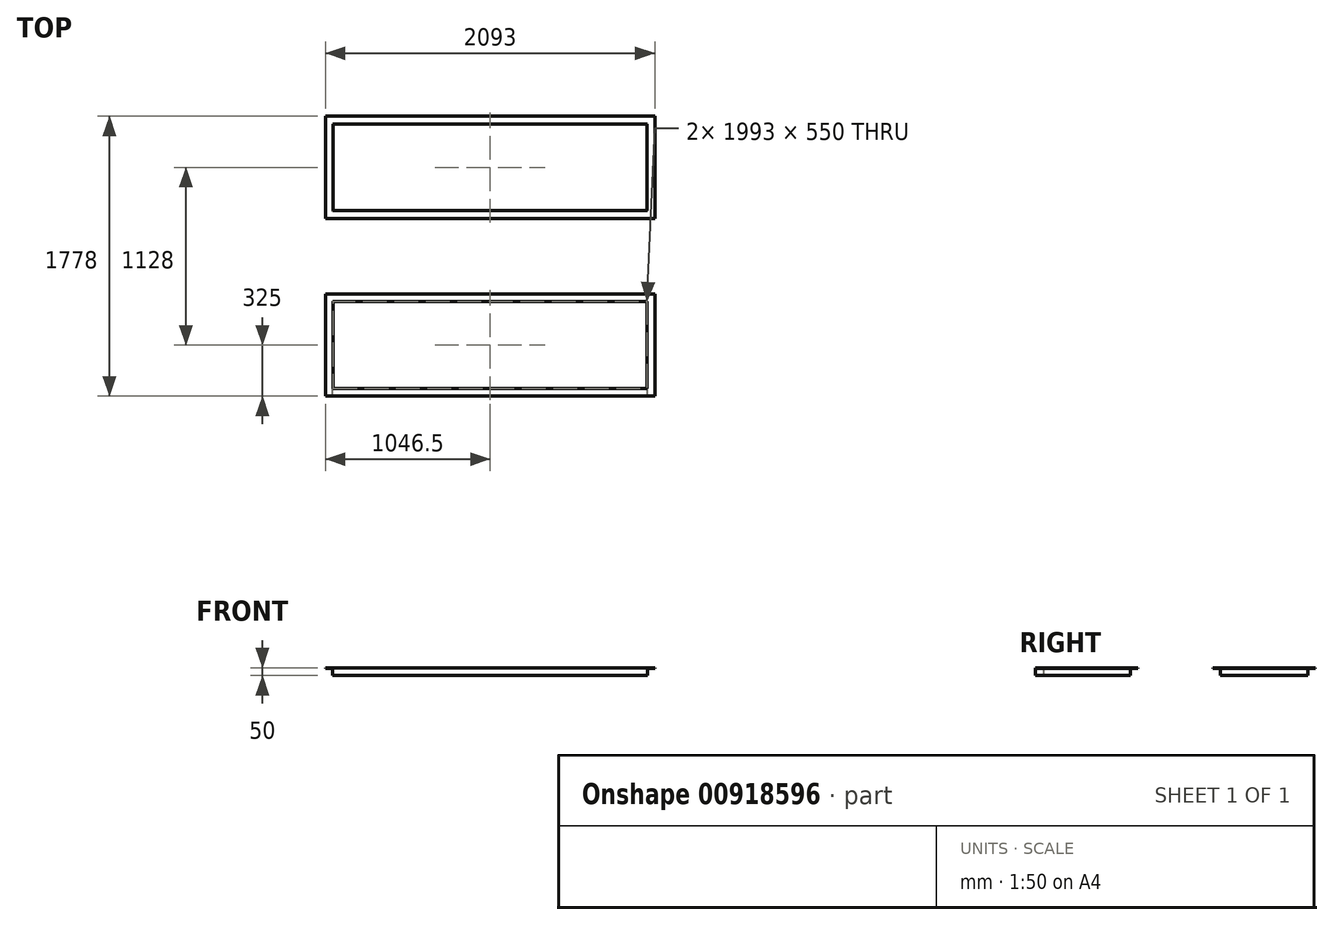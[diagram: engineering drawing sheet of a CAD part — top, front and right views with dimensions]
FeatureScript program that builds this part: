
annotation { "Feature Type Name" : "Feature", "Feature Type Description" : "" }
export const myFeature = defineFeature(function(context is Context, id is Id, definition is map)
    precondition{}
    {
        {
            var Q0;
            Q0=qCreatedBy(makeId("Top.planeOp"),FACE);
            var sketch = newSketch(context, id + "F0", { "sketchPlane" : qUnion([Q0])});
            skLineSegment(sketch, "E0.bottom", {"start": v(0, 0) * mm, "end": v(-1993, 0) * mm});
            skLineSegment(sketch, "E0.top", {"start": v(0, 550) * mm, "end": v(-1993, 550) * mm});
            skLineSegment(sketch, "E0.left", {"start": v(0, 0) * mm, "end": v(0, 550) * mm});
            skLineSegment(sketch, "E0.right", {"start": v(-1993, 0) * mm, "end": v(-1993, 550) * mm});
            skLineSegment(sketch, "E1.bottom", {"start": v(-2043, 600) * mm, "end": v(50, 600) * mm});
            skLineSegment(sketch, "E1.top", {"start": v(-2043, -50) * mm, "end": v(50, -50) * mm});
            skLineSegment(sketch, "E1.left", {"start": v(-2043, 600) * mm, "end": v(-2043, -50) * mm});
            skLineSegment(sketch, "E1.right", {"start": v(50, 600) * mm, "end": v(50, -50) * mm});
            skLineSegment(sketch, "E2.bottom", {"start": v(-1993, 1128) * mm, "end": v(0, 1128) * mm});
            skLineSegment(sketch, "E2.top", {"start": v(-1993, 1678) * mm, "end": v(0, 1678) * mm});
            skLineSegment(sketch, "E2.left", {"start": v(-1993, 1128) * mm, "end": v(-1993, 1678) * mm});
            skLineSegment(sketch, "E2.right", {"start": v(0, 1128) * mm, "end": v(0, 1678) * mm});
            skLineSegment(sketch, "E3.bottom", {"start": v(-2043, 1078) * mm, "end": v(50, 1078) * mm});
            skLineSegment(sketch, "E3.top", {"start": v(-2043, 1728) * mm, "end": v(50, 1728) * mm});
            skLineSegment(sketch, "E3.left", {"start": v(-2043, 1078) * mm, "end": v(-2043, 1728) * mm});
            skLineSegment(sketch, "E3.right", {"start": v(50, 1078) * mm, "end": v(50, 1728) * mm});
            skSolve(sketch);
        }
        {
            var Q0;
            Q0 = qSketchRegion(id + "F0", true);
            extrude(context, id + "F1", {"entities" : qUnion([Q0]), "depth" : 50 * mm, "offsetDistance" : 25 * mm});
        }
        {
            var Q0;
            Q0=makeQuery(id+"F1.opExtrude","SWEPT_FACE",FACE,{"disambiguationData":[OSD([sQuery(id+"F0.wireOp",EDGE,"E3.left")])]});
            var sketch = newSketch(context, id + "F2", { "sketchPlane" : qUnion([Q0])});
            skLineSegment(sketch, "E4.bottom", {"start": v(-1728, 46) * mm, "end": v(-1682, 46) * mm});
            skLineSegment(sketch, "E4.top", {"start": v(-1728, 0) * mm, "end": v(-1682, 0) * mm});
            skLineSegment(sketch, "E4.left", {"start": v(-1728, 46) * mm, "end": v(-1728, 0) * mm});
            skLineSegment(sketch, "E4.right", {"start": v(-1682, 46) * mm, "end": v(-1682, 0) * mm});
            skLineSegment(sketch, "E5.bottom", {"start": v(-1078, 46) * mm, "end": v(-1124, 46) * mm});
            skLineSegment(sketch, "E5.top", {"start": v(-1078, 0) * mm, "end": v(-1124, 0) * mm});
            skLineSegment(sketch, "E5.left", {"start": v(-1078, 46) * mm, "end": v(-1078, 0) * mm});
            skLineSegment(sketch, "E5.right", {"start": v(-1124, 46) * mm, "end": v(-1124, 0) * mm});
            skLineSegment(sketch, "E6.0.0", {"start": v(-600, 0) * mm, "end": v(50, 0) * mm});
            skLineSegment(sketch, "E6.0.1", {"start": v(50, 0) * mm, "end": v(50, 50) * mm});
            skLineSegment(sketch, "E6.0.2", {"start": v(50, 50) * mm, "end": v(-600, 50) * mm});
            skLineSegment(sketch, "E6.0.3", {"start": v(-600, 50) * mm, "end": v(-600, 0) * mm});
            skLineSegment(sketch, "E7.bottom", {"start": v(-600, 46) * mm, "end": v(-554, 46) * mm});
            skLineSegment(sketch, "E7.top", {"start": v(-600, 0) * mm, "end": v(-554, 0) * mm});
            skLineSegment(sketch, "E7.left", {"start": v(-600, 46) * mm, "end": v(-600, 0) * mm});
            skLineSegment(sketch, "E7.right", {"start": v(-554, 46) * mm, "end": v(-554, 0) * mm});
            skLineSegment(sketch, "E8.bottom", {"start": v(4, 0) * mm, "end": v(50, 0) * mm});
            skLineSegment(sketch, "E8.top", {"start": v(4, 46) * mm, "end": v(50, 46) * mm});
            skLineSegment(sketch, "E8.left", {"start": v(4, 0) * mm, "end": v(4, 46) * mm});
            skLineSegment(sketch, "E8.right", {"start": v(50, 0) * mm, "end": v(50, 46) * mm});
            skSolve(sketch);
        }
        {
            var Q0;
            Q0=makeQuery(id+"F2.imprint","IMPRINT",FACE,{"disambiguationData":[TD([[makeQuery(id+"F2.imprint","IMPRINT",EDGE,{"derivedFrom":sQuery(id+"F2.wireOp",EDGE,"E4.bottom")}),-1.0]])]});
            var Q1;
            Q1=makeQuery(id+"F2.imprint","IMPRINT",FACE,{"disambiguationData":[TD([[makeQuery(id+"F2.imprint","IMPRINT",EDGE,{"derivedFrom":sQuery(id+"F2.wireOp",EDGE,"E5.bottom")}),1.0]])]});
            var Q2;
            Q2=makeQuery(id+"F2.imprint","IMPRINT",FACE,{"disambiguationData":[TD([[makeQuery(id+"F2.imprint","IMPRINT",EDGE,{"derivedFrom":sQuery(id+"F2.wireOp",EDGE,"E7.bottom")}),-1.0]])]});
            var Q3;
            Q3=makeQuery(id+"F2.imprint","IMPRINT",FACE,{"disambiguationData":[TD([[makeQuery(id+"F2.imprint","IMPRINT",EDGE,{"derivedFrom":sQuery(id+"F2.wireOp",EDGE,"E8.bottom")}),1.0]])]});
            extrude(context, id + "F3", {"entities" : qUnion([Q0, Q1, Q2, Q3]), "operationType" : NewBodyOperationType.REMOVE, "oppositeDirection" : true, "depth" : 3000 * mm, "offsetDistance" : 25 * mm});
        }
        {
            var Q0;
            Q0=makeQuery(id+"F3.boolean.opBoolean","COPY",FACE,{"derivedFrom":makeQuery(id+"F3.opExtrude","SWEPT_FACE",FACE,{"disambiguationData":[OSD([sQuery(id+"F2.wireOp",EDGE,"E4.right")])]})});
            var sketch = newSketch(context, id + "F4", { "sketchPlane" : qUnion([Q0])});
            skLineSegment(sketch, "E9.bottom", {"start": v(-50, 46) * mm, "end": v(-4, 46) * mm});
            skLineSegment(sketch, "E9.top", {"start": v(-50, 0) * mm, "end": v(-4, 0) * mm});
            skLineSegment(sketch, "E9.left", {"start": v(-50, 46) * mm, "end": v(-50, 0) * mm});
            skLineSegment(sketch, "E9.right", {"start": v(-4, 46) * mm, "end": v(-4, 0) * mm});
            skLineSegment(sketch, "E10.bottom", {"start": v(2043, 46) * mm, "end": v(1997, 46) * mm});
            skLineSegment(sketch, "E10.top", {"start": v(2043, 0) * mm, "end": v(1997, 0) * mm});
            skLineSegment(sketch, "E10.left", {"start": v(2043, 46) * mm, "end": v(2043, 0) * mm});
            skLineSegment(sketch, "E10.right", {"start": v(1997, 46) * mm, "end": v(1997, 0) * mm});
            skSolve(sketch);
        }
        {
            var Q0;
            Q0 = qSketchRegion(id + "F4", true);
            extrude(context, id + "F5", {"entities" : qUnion([Q0]), "operationType" : NewBodyOperationType.REMOVE, "oppositeDirection" : true, "depth" : 3000 * mm, "offsetDistance" : 25 * mm});
        }
    });
